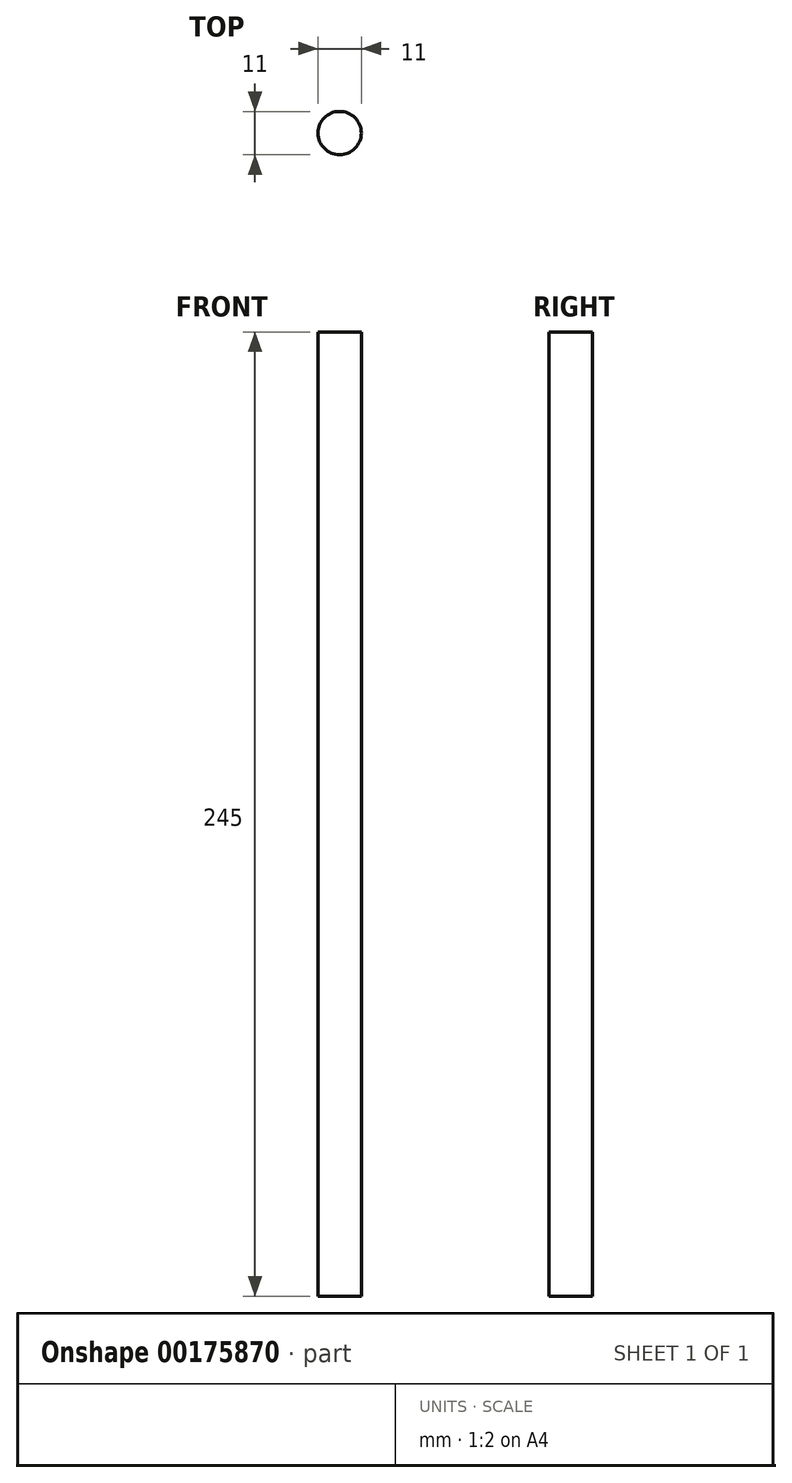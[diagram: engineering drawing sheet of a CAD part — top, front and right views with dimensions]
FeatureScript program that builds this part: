
annotation { "Feature Type Name" : "Feature", "Feature Type Description" : "" }
export const myFeature = defineFeature(function(context is Context, id is Id, definition is map)
    precondition{}
    {
        {
            var Q0;
            Q0=qCreatedBy(makeId("Top.planeOp"),FACE);
            var sketch = newSketch(context, id + "F0", { "sketchPlane" : qUnion([Q0])});
            skCircle(sketch, "E0", {"center": v(-72.82, -11.12) * mm, "radius": 5.5 * mm});
            skSolve(sketch);
        }
        {
            var Q0;
            Q0=qSketchRegion(id+"F0",true);
            extrude(context, id + "F1", {"entities" : qUnion([Q0]), "depth" : 245 * mm});
        }
    });
